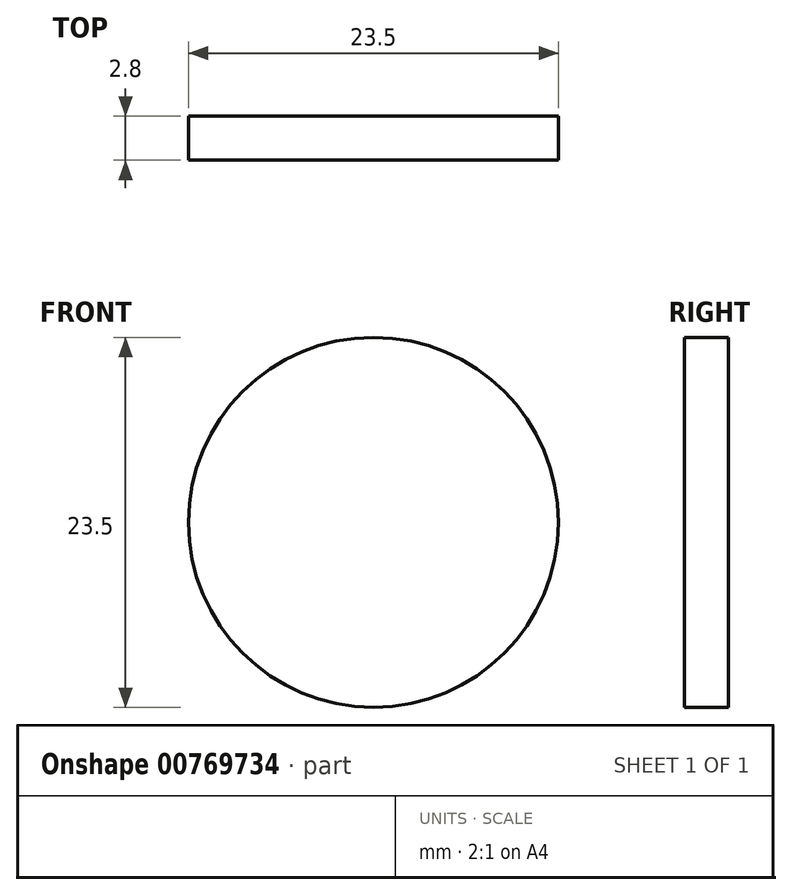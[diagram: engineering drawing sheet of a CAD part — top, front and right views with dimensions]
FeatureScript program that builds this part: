
annotation { "Feature Type Name" : "Feature", "Feature Type Description" : "" }
export const myFeature = defineFeature(function(context is Context, id is Id, definition is map)
    precondition{}
    {
        {
            var Q0;
            Q0=qCreatedBy(makeId("Front.planeOp"),FACE);
            var sketch = newSketch(context, id + "F0", { "sketchPlane" : qUnion([Q0])});
            skCircle(sketch, "E0", {"center": v(0, 0) * mm, "radius": 11.75 * mm});
            skSolve(sketch);
        }
        {
            var Q0;
            Q0 = qSketchRegion(id + "F0", true);
            extrude(context, id + "F1", {"entities" : qUnion([Q0]), "depth" : 2.8 * mm, "offsetDistance" : 25 * mm});
        }
    });
